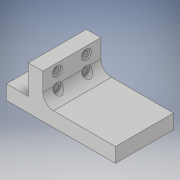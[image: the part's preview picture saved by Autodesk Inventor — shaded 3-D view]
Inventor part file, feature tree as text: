
AUTODESK INVENTOR PART (.ipt)
format: ipt  version: 2019 (Build 230136000, 136)  size: 142,336 bytes
history: native  units: mm
features: sketch x2, extrude x1, hole x1, fillet x1
ambient origin geometry x8: Origin, YZ Plane, XZ Plane, XY Plane, X Axis, Y Axis, Z Axis, Center Point
bodies: Solid1 (feature_tree)
feature tree (5):
  extrude  "Extrusion1"  Depth=10.0mm
  hole  "Hole1"  [1 undecoded]
  fillet  "Fillet3"  Radius=50.0mm
  sketch  "Sketch1"  dims[d0=10.0mm d1=20.0mm]
  sketch  "Sketch2"  dims[d2=25.0mm d3=10.0mm d4=50.0mm d5=40.0mm d6=0.0mm d9=20.0mm d10=3.9mm d11=6.0mm d12=6.75mm d13=1.0mm d14=90.0deg d15=8.0mm d16=90.0deg d17=7.25mm]
note: 1 required parameter value undecoded (feature->parameter linkage not recoverable at this tier; creation-order binding heuristic only, values carry confidence <= 0.55)
